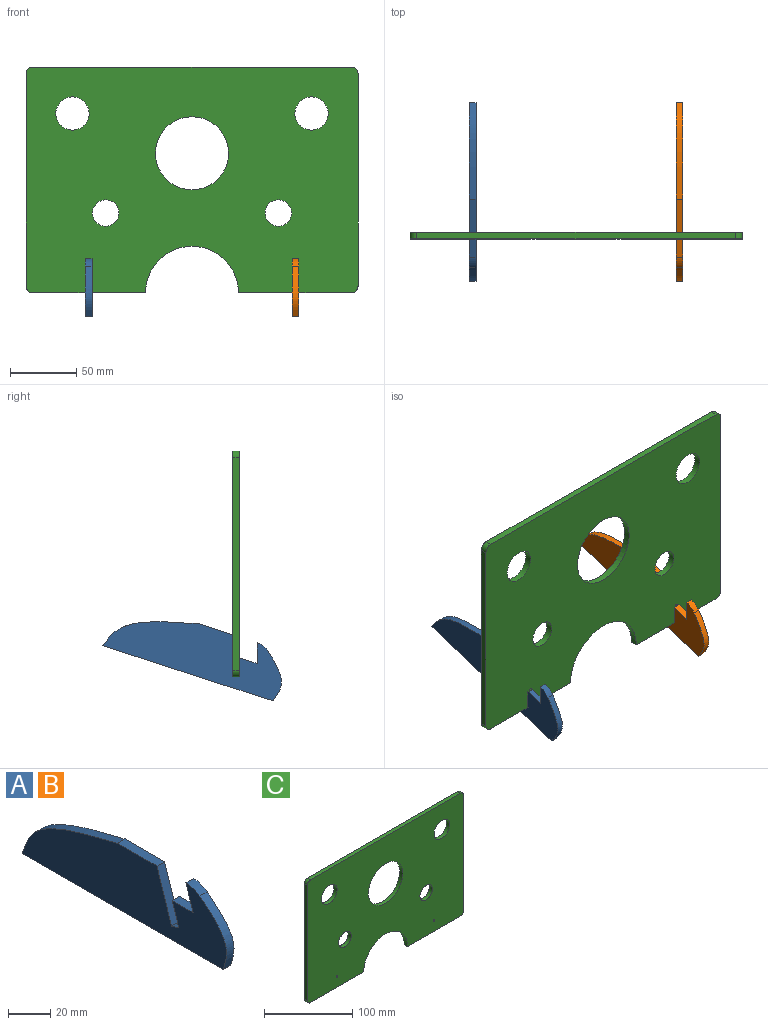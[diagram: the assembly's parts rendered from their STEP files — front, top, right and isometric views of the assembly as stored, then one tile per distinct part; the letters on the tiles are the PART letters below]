
ASSEMBLY  parts=3 mates=2
PART A: 12 faces, bbox 5x138.6x38 mm
  f0: plane 14.09x5mm, normal (0,0,1), area 70.4mm2, adj f1,f9,f10,f11
  f1: plane 15x5mm, normal (0,0.95,-0.31), area 78.9mm2, adj f0,f2,f10,f11
  f2: cylinder r=15mm len=9.22mm, axis (-1,0,0), area 49.6mm2, adj f1,f3,f10,f11
  f3: extruded ~34.83x18.09mm, area 210.9mm2, adj f2,f4,f10,f11
  f4: plane 135x5mm, normal (0,0,-1), area 675mm2, adj f3,f5,f10,f11
  f5: extruded ~64.16x38mm, area 394.9mm2, adj f4,f6,f10,f11
  f6: plane 26.5x5mm, normal (0,0,1), area 132.5mm2, adj f5,f7,f10,f11
  f7: plane 30.08x9.77mm, normal (0,-0.95,0.31), area 158.1mm2, adj f6,f8,f10,f11
  f8: plane 5x4.76mm, normal (0,0.31,0.95), area 25mm2, adj f7,f9,f10,f11
  f9: plane 13.53x5mm, normal (0,0.95,-0.31), area 71.1mm2, adj f0,f8,f10,f11
  f10: plane 138.58x38mm, normal (1,0,0), area 3920.6mm2, adj f0,f1,f2,f3,f4,f5,f6,f7
  f11: plane 138.58x38mm, normal (-1,0,0), area 3920.6mm2, adj f0,f1,f2,f3,f4,f5,f6,f7
PART B: same geometry as A
PART C: 19 faces, bbox 250x5x170 mm
  f0: plane 240x5mm, normal (0,0,1), area 1200mm2, adj f1,f16,f17,f18
  f1: cylinder r=5mm len=5mm, axis (0,1,0), area 39.3mm2, adj f0,f2,f17,f18
  f2: plane 160x5mm, normal (-1,0,0), area 800mm2, adj f1,f3,f17,f18
  f3: cylinder r=5mm len=5mm, axis (0,1,0), area 39.3mm2, adj f2,f4,f17,f18
  f4: plane 85x5mm, normal (0,0,-1), area 425mm2, adj f3,f5,f17,f18
  f5: cylinder r=35mm len=70mm, axis (0,1,0), area 549.8mm2, adj f4,f6,f17,f18
  f6: plane 85x5mm, normal (0,0,-1), area 425mm2, adj f5,f7,f17,f18
  f7: cylinder r=5mm len=5mm, axis (0,1,0), area 39.3mm2, adj f6,f8,f17,f18
  f8: plane 160x5mm, normal (1,0,0), area 800mm2, adj f7,f16,f17,f18
  f9: cylinder r=12.5mm len=25mm, axis (0,1,0), area 392.7mm2, adj f17,f18
  f10: cylinder r=10mm len=20mm, axis (0,1,0), area 314.2mm2, adj f17,f18
  f11: cylinder r=1mm len=5mm, axis (0,1,0), area 31.4mm2, adj f17,f18
  f12: cylinder r=27.5mm len=55mm, axis (0,1,0), area 863.9mm2, adj f17,f18
  f13: cylinder r=1mm len=5mm, axis (0,1,0), area 31.4mm2, adj f17,f18
  f14: cylinder r=10mm len=20mm, axis (0,1,0), area 314.2mm2, adj f17,f18
  f15: cylinder r=12.5mm len=25mm, axis (0,1,0), area 392.7mm2, adj f17,f18
  f16: cylinder r=5mm len=5mm, axis (0,1,0), area 39.3mm2, adj f0,f8,f17,f18
  f17: plane 250x170mm, normal (0,-1,0), area 36562.1mm2, adj f0,f1,f2,f3,f4,f5,f6,f7
  f18: plane 250x170mm, normal (0,1,0), area 36562.1mm2, adj f0,f1,f2,f3,f4,f5,f6,f7
PLACE A rot(axis=(1,0,0),18deg) t=(-12.57,120.94,116.55)mm
PLACE B rot(axis=(1,0,0),18deg) t=(143.22,120.94,116.55)mm
PLACE C t=(67.69,89.86,179.8)mm
MATE pin_slot A.f8 <-> C.f4  axis (0,0,1) through (-10.07,87.36,94.8)mm
MATE pin_slot B.f8 <-> C.f4  axis (0,0,1) through (145.72,87.36,94.8)mm
